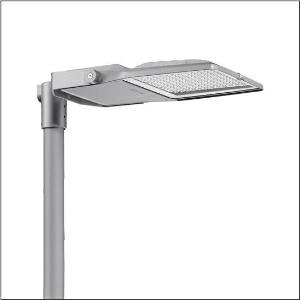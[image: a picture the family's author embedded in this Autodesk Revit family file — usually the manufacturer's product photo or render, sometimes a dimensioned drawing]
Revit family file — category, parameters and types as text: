
# Revit family: floodlight_fl_21_iq_midi___pl64_5xa7782f4e3a_0b41
name_source: partatom
category: Lighting Fixtures
units: mm (PartAtom-declared; Revit-internal decimal feet)

## family parameters
Cut with Voids When Loaded = No
Host = Face
Light Source = No
Part Type = Normal
Room Calculation Point = No
Round Connector Dimension = Use Diameter
Shared = No

## types (1)
- --- (1 x LED, 36050 lm, 270.2 W, 4000K)
    Apparent Load = 270 VA
    CIE Flux Codes = 28 80 98 100 100
    Color Rendering = 70
    Color Temperature = 4000K
    Default Elevation = 1800 mm
    Description = Floodlight FL 21 iQ midi, floodlight, primary light control with lens, of PMMA, primary optical cover: protective disc, of toughened safety glass, transparent, light distribution: PL64, light emission: direct distribution, installation type: surface-mounted, LED, High Power LED, rated luminous flux: 36.050lm, luminous efficacy: 133lm/W, light colour: 740, colour temperature: 4000K, control gear: ECG iQ, control: optimised constant luminous flux control (CLO 2.0), Desk-Remote (wireless, voltage-free reading and setting of iQ features in the workshop via application-optimized NFC function/RFID function), Smart-Wire, Night-Set, Temp-Guard, Auto-Match, Street-Remote, with terminal, 6-pole, mains connection: 220..240V, AC, 50/60Hz, start of lifetime: 270W, end of service life: 287W, reduction: 118W, luminaire housing, of diecast aluminium, powder-coated, Siteco® metallic grey (DB 702S), corrosivity category C5 mid according to DIN EN ISO 12944, sealing non-destructively replaceable, please order mast flange separately, mast bracket, of steel, galvanised, powder-coated, Siteco® metallic grey (DB 702S), protection rating (complete): IP66, insulation class (complete): insulation class II (safety insulation), certification: CE, protection symbol: D, impact resistance: IK08, permissible operating ambient temperature: -40..+40°C, permissible operating ambient temperature for outdoor applications: -40..+50°C, standard: DIN EN 12944, LABS conformity tested according to VDMA 24364:2018-05, packaging unit: 1 piece

Light Distribution: PL64
    Height = 76 mm
    Lamp = 1 x LED
    Lamp Light Flux = 36050 lm
    Lamp Power = 270.2 W
    Lamp count = 1
    Length = 657 mm
    Luminous efficacy = 133 lm/W
    Manufacturer = Siteco
    ModVariant = No
    Model = 5XA7782F4E3A
    Number of Poles = 1
    OnlyDefault = Yes
    Power Factor = 1
    Product Name = Floodlight FL 21 iQ midi | PL64
    Product group = floodlight | pylon annexe
    ProductGroupID = 6200
    Protection Class = Protection class II
    Protection Degree = IP 66
    RLX_Detail_Level = 1
    RLX_Emergency_Light_Flux = 0 lm
    RLX_Emergency_Type = 0
    RLX_Emergency_Type_DB = No
    RlxData = <blob elided: 153813 chars, md5=c2e05ba7>
    Socket = socket
    Standby Power = 0 W
    System Light Flux = 36050 lm
    System Power = 270 W
    Type Comments = factory setting: luminous flux: 100 % | dim-lin: 254 | 620 mA
    Type Image = l_1007123.jpg
    URL = http://relux.com
    VarID = @adj_054849
    Voltage = 0 V
    Weight = 0.00 kg
    Width = 442 mm

## geometry (parser evidence)
native form markers: Blend x4, Sweep x14
no freeform markers — native parametric forms only
